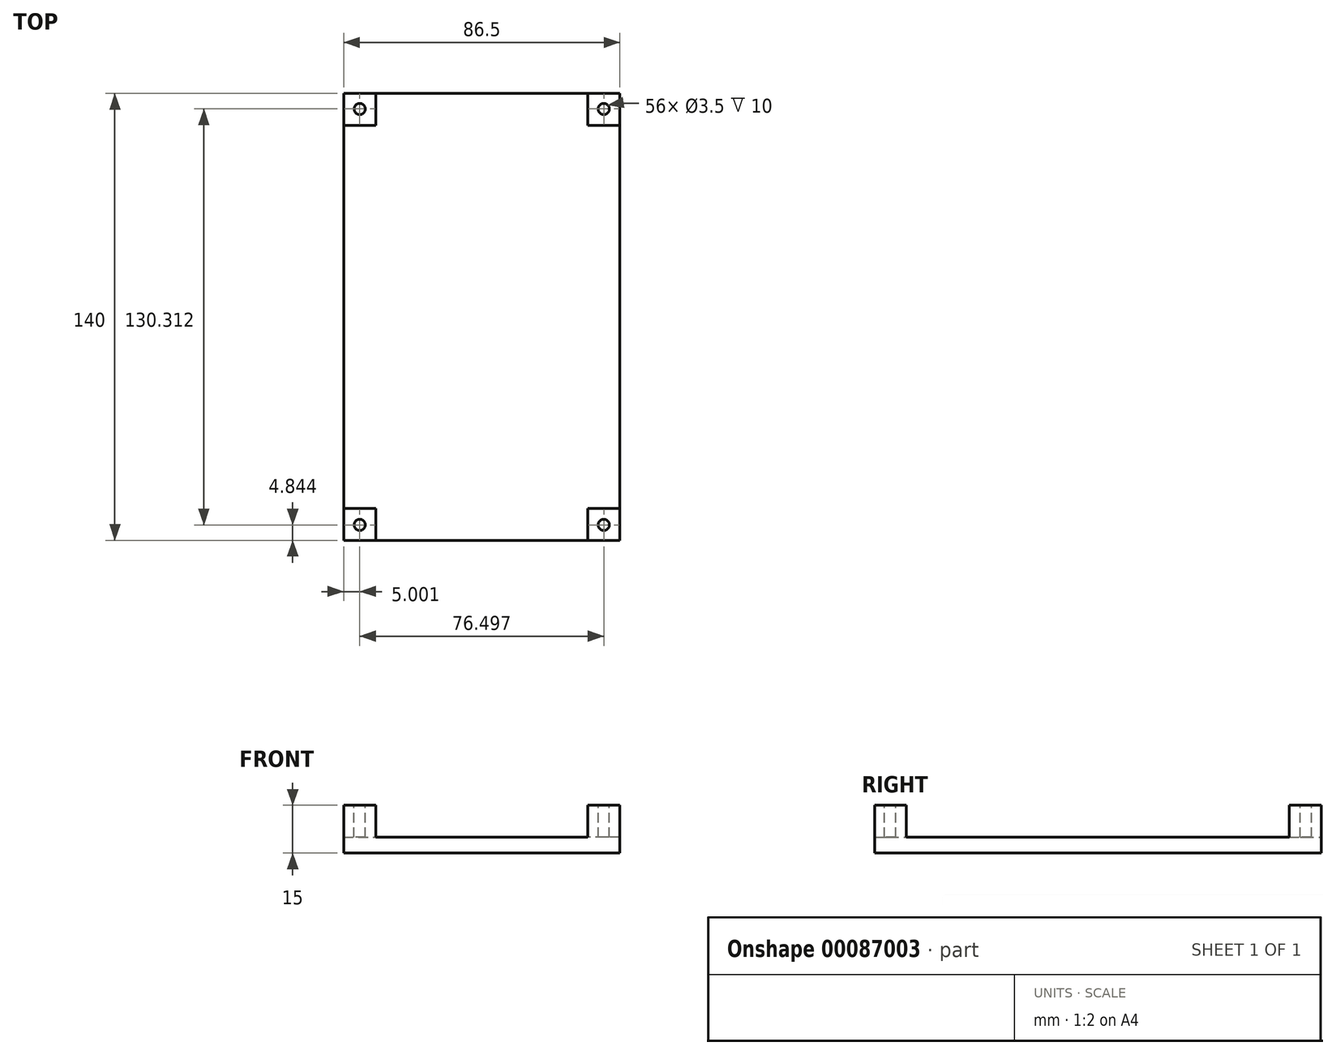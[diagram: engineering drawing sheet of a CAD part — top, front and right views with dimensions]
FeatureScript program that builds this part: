
annotation { "Feature Type Name" : "Feature", "Feature Type Description" : "" }
export const myFeature = defineFeature(function(context is Context, id is Id, definition is map)
    precondition{}
    {
        {
            var Q0;
            Q0=qCreatedBy(makeId("Top.planeOp"),FACE);
            var sketch = newSketch(context, id + "F0", { "sketchPlane" : qUnion([Q0])});
            skLineSegment(sketch, "E0.bottom", {"start": v(43.25, 70) * mm, "end": v(-43.25, 70) * mm});
            skLineSegment(sketch, "E0.top", {"start": v(43.25, -70) * mm, "end": v(-43.25, -70) * mm});
            skLineSegment(sketch, "E0.left", {"start": v(43.25, 70) * mm, "end": v(43.25, -70) * mm});
            skLineSegment(sketch, "E0.right", {"start": v(-43.25, 70) * mm, "end": v(-43.25, -70) * mm});
            skPoint(sketch, "E0.middle", {"position": v(0, 0) * mm});
            skSolve(sketch);
        }
        {
            var Q0;
            Q0=makeQuery(id+"F0.imprint","IMPRINT",FACE,{"disambiguationData":[TD([[makeQuery(id+"F0.imprint","IMPRINT",EDGE,{"derivedFrom":sQuery(id+"F0.wireOp",EDGE,"E0.bottom")}),1.0]])]});
            extrude(context, id + "F1", {"entities" : qUnion([Q0]), "depth" : 15 * mm});
        }
        {
            var Q0;
            Q0=makeQuery(id+"F1.opExtrude","CAP_FACE",FACE,{"disambiguationData":[OSD([sQuery(id+"F0.wireOp",EDGE,"E0.bottom"),sQuery(id+"F0.wireOp",EDGE,"E0.top"),sQuery(id+"F0.wireOp",EDGE,"E0.left"),sQuery(id+"F0.wireOp",EDGE,"E0.right")])],"isStart":false});
            var sketch = newSketch(context, id + "F2", { "sketchPlane" : qUnion([Q0])});
            skLineSegment(sketch, "E1.bottom", {"start": v(33.25, -70) * mm, "end": v(-33.25, -70) * mm});
            skLineSegment(sketch, "E1.top", {"start": v(33.25, 70) * mm, "end": v(-33.25, 70) * mm});
            skLineSegment(sketch, "E1.left", {"start": v(33.25, -70) * mm, "end": v(33.25, 70) * mm});
            skLineSegment(sketch, "E1.right", {"start": v(-33.25, -70) * mm, "end": v(-33.25, 70) * mm});
            skPoint(sketch, "E1.middle", {"position": v(0, 0) * mm});
            skLineSegment(sketch, "E2.bottom", {"start": v(-43.25, 60) * mm, "end": v(-33.25, 60) * mm});
            skLineSegment(sketch, "E2.top", {"start": v(-43.25, -60) * mm, "end": v(-33.25, -60) * mm});
            skLineSegment(sketch, "E2.left", {"start": v(-43.25, 60) * mm, "end": v(-43.25, -60) * mm});
            skLineSegment(sketch, "E2.right", {"start": v(-33.25, 60) * mm, "end": v(-33.25, -60) * mm});
            skPoint(sketch, "E2.middle", {"position": v(-38.25, 0) * mm});
            skPoint(sketch, "E2.middle.positionSnap0", {"position": v(-43.25, 0) * mm});
            skPoint(sketch, "E2.centerSnap0", {"position": v(-43.25, 0) * mm});
            skLineSegment(sketch, "E3.MirrorCS", {"start": v(43.25, 60) * mm, "end": v(43.25, -60) * mm});
            skLineSegment(sketch, "E4.MirrorCS", {"start": v(43.25, 60) * mm, "end": v(33.25, 60) * mm});
            skLineSegment(sketch, "E5.MirrorCS", {"start": v(43.25, -60) * mm, "end": v(33.25, -60) * mm});
            skCircle(sketch, "E6", {"center": v(-38.25, 65.16) * mm, "radius": 1.75 * mm});
            skCircle(sketch, "E7.MirrorC", {"center": v(38.25, 65.16) * mm, "radius": 1.75 * mm});
            skCircle(sketch, "E8.MirrorC", {"center": v(-38.25, -65.16) * mm, "radius": 1.75 * mm});
            skCircle(sketch, "E9.MirrorC", {"center": v(38.25, -65.16) * mm, "radius": 1.75 * mm});
            skSolve(sketch);
        }
        {
            var Q0;
            Q0 = qSketchRegion(id + "F2", true);
            extrude(context, id + "F3", {"entities" : qUnion([Q0]), "operationType" : NewBodyOperationType.REMOVE, "oppositeDirection" : true, "depth" : 10 * mm});
        }
    });
